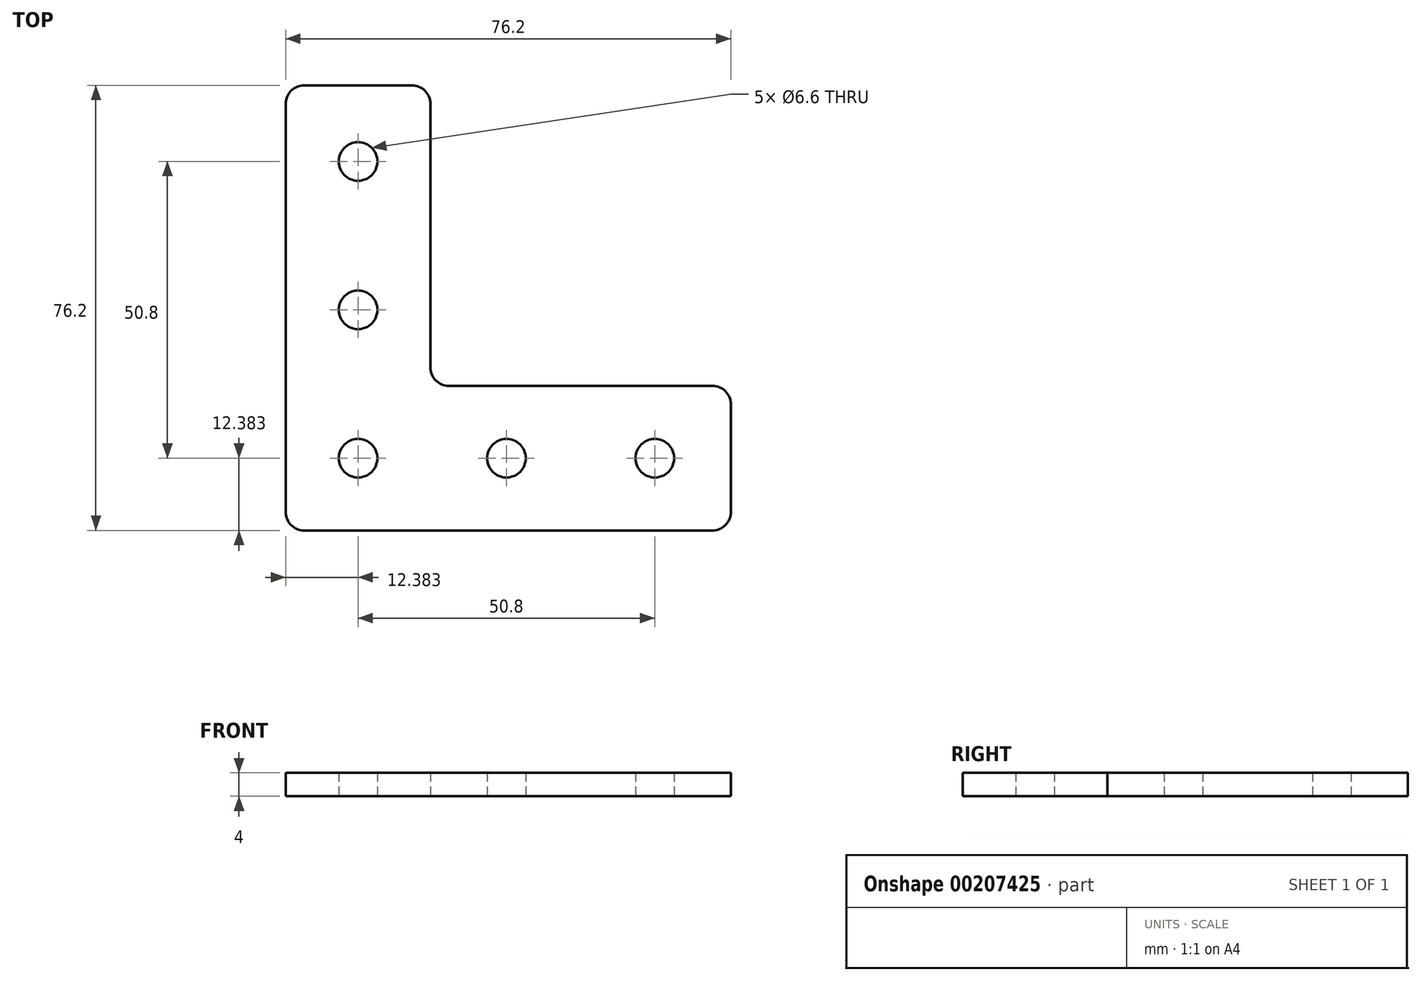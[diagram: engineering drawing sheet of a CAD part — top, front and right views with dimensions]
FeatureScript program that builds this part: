
annotation { "Feature Type Name" : "Feature", "Feature Type Description" : "" }
export const myFeature = defineFeature(function(context is Context, id is Id, definition is map)
    precondition{}
    {
        {
            var Q0;
            Q0=qCreatedBy(makeId("Top.planeOp"),FACE);
            var sketch = newSketch(context, id + "F0", { "sketchPlane" : qUnion([Q0])});
            skLineSegment(sketch, "E0", {"start": v(0, 76.2) * mm, "end": v(0, 0) * mm});
            skLineSegment(sketch, "E1", {"start": v(0, 0) * mm, "end": v(76.2, 0) * mm});
            skLineSegment(sketch, "E2.0", {"start": v(24.77, 24.77) * mm, "end": v(76.2, 24.77) * mm});
            skLineSegment(sketch, "E2.1", {"start": v(24.77, 76.2) * mm, "end": v(24.77, 24.77) * mm});
            skLineSegment(sketch, "E3", {"start": v(0, 76.2) * mm, "end": v(24.77, 76.2) * mm});
            skLineSegment(sketch, "E4", {"start": v(76.2, 0) * mm, "end": v(76.2, 24.77) * mm});
            skCircle(sketch, "E5", {"center": v(12.38, 12.38) * mm, "radius": 3.3 * mm});
            skPoint(sketch, "E5.centerSnap0", {"position": v(76.2, 12.38) * mm});
            skPoint(sketch, "E5.centerSnap1", {"position": v(12.38, 76.2) * mm});
            skCircle(sketch, "E6.1.0.0", {"center": v(37.78, 12.38) * mm, "radius": 3.3 * mm});
            skCircle(sketch, "E6.2.0.0", {"center": v(63.18, 12.38) * mm, "radius": 3.3 * mm});
            skLineSegment(sketch, "E6.direction1", {"start": v(12.38, 12.38) * mm, "end": v(37.78, 12.38) * mm, "construction": true});
            skCircle(sketch, "E7.0.1.0", {"center": v(12.38, 37.78) * mm, "radius": 3.3 * mm});
            skCircle(sketch, "E7.0.2.0", {"center": v(12.38, 63.18) * mm, "radius": 3.3 * mm});
            skLineSegment(sketch, "E7.direction2", {"start": v(12.38, 12.38) * mm, "end": v(12.38, 37.78) * mm, "construction": true});
            skSolve(sketch);
        }
        {
            var Q0;
            Q0 = qSketchRegion(id + "F0", true);
            extrude(context, id + "F1", {"entities" : qUnion([Q0]), "depth" : 4 * mm});
        }
        {
            var Q0;
            Q0=makeQuery(id+"F1.opExtrude","SWEPT_EDGE",EDGE,{"disambiguationData":[OSD([sQuery(id+"F0.wireOp",EDGE,"E2.0"),sQuery(id+"F0.wireOp",EDGE,"E2.1")])]});
            var Q1;
            Q1=makeQuery(id+"F1.opExtrude","SWEPT_EDGE",EDGE,{"disambiguationData":[OSD([sQuery(id+"F0.wireOp",EDGE,"E2.0"),sQuery(id+"F0.wireOp",EDGE,"E4")])]});
            var Q2;
            Q2=makeQuery(id+"F1.opExtrude","SWEPT_EDGE",EDGE,{"disambiguationData":[OSD([sQuery(id+"F0.wireOp",EDGE,"E1"),sQuery(id+"F0.wireOp",EDGE,"E4")])]});
            var Q3;
            Q3=makeQuery(id+"F1.opExtrude","SWEPT_EDGE",EDGE,{"disambiguationData":[OSD([sQuery(id+"F0.wireOp",EDGE,"E0"),sQuery(id+"F0.wireOp",EDGE,"E1")])]});
            var Q4;
            Q4=makeQuery(id+"F1.opExtrude","SWEPT_EDGE",EDGE,{"disambiguationData":[OSD([sQuery(id+"F0.wireOp",EDGE,"E2.1"),sQuery(id+"F0.wireOp",EDGE,"E3")])]});
            var Q5;
            Q5=makeQuery(id+"F1.opExtrude","SWEPT_EDGE",EDGE,{"disambiguationData":[OSD([sQuery(id+"F0.wireOp",EDGE,"E0"),sQuery(id+"F0.wireOp",EDGE,"E3")])]});
            fillet(context, id + "F2", {"entities" : qUnion([Q0, Q1, Q2, Q3, Q4, Q5]), "radius" : 3.17 * mm, "tangentPropagation" : true, "allowEdgeOverflow" : false});
        }
    });
